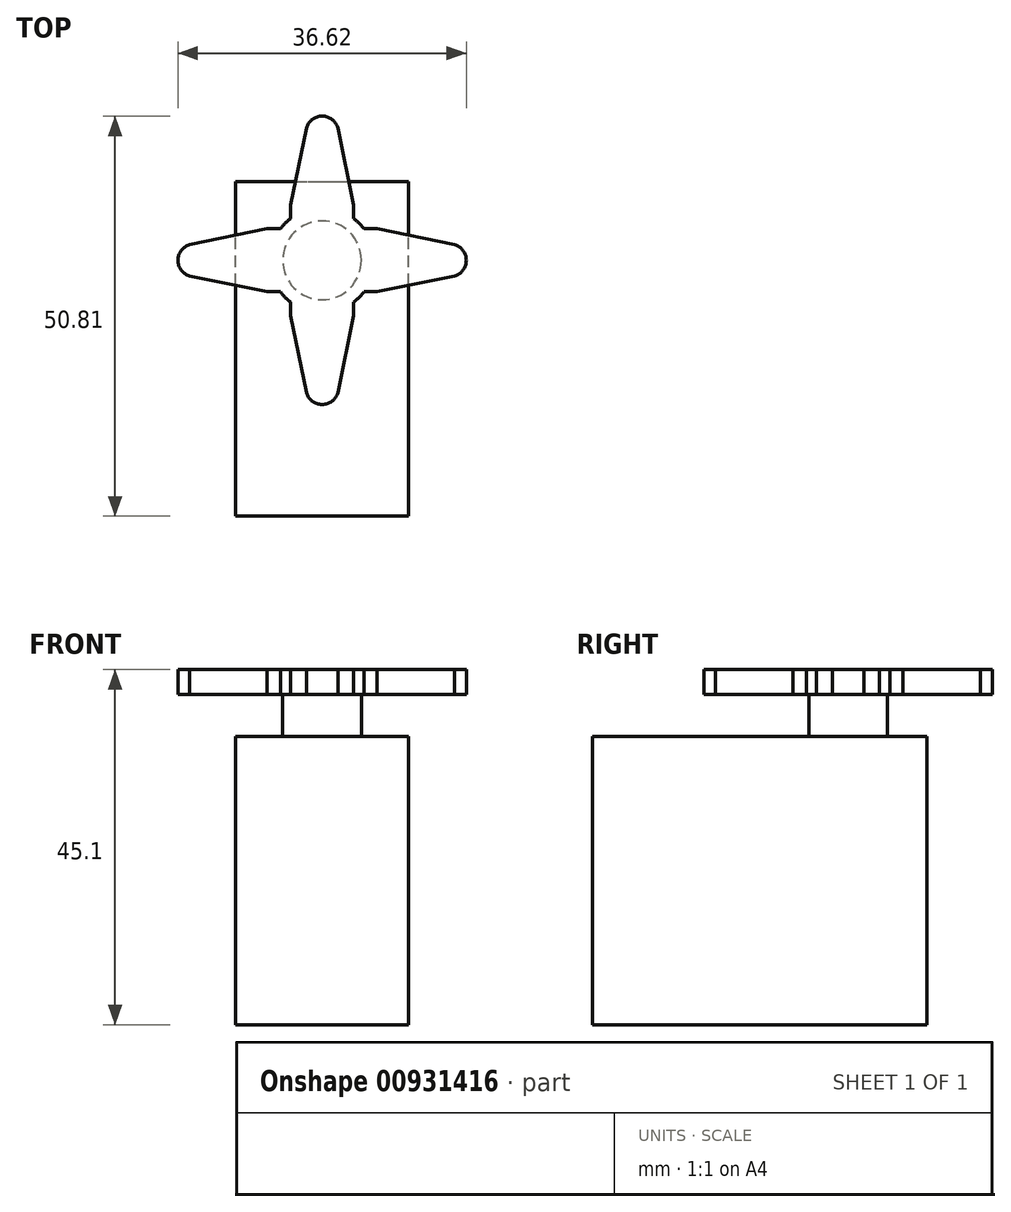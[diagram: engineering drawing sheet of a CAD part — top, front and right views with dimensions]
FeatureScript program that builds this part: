
annotation { "Feature Type Name" : "Feature", "Feature Type Description" : "" }
export const myFeature = defineFeature(function(context is Context, id is Id, definition is map)
    precondition{}
    {
        {
            var Q0;
            Q0=qCreatedBy(makeId("Top.planeOp"),FACE);
            var sketch = newSketch(context, id + "F0", { "sketchPlane" : qUnion([Q0])});
            skLineSegment(sketch, "E0.bottom", {"start": v(0, 0) * mm, "end": v(22, 0) * mm});
            skLineSegment(sketch, "E0.top", {"start": v(0, 42.5) * mm, "end": v(22, 42.5) * mm});
            skLineSegment(sketch, "E0.left", {"start": v(0, 0) * mm, "end": v(0, 42.5) * mm});
            skLineSegment(sketch, "E0.right", {"start": v(22, 0) * mm, "end": v(22, 42.5) * mm});
            skSolve(sketch);
        }
        {
            var Q0;
            Q0=makeQuery(id+"F0.imprint","IMPRINT",FACE,{"disambiguationData":[TD([[makeQuery(id+"F0.imprint","IMPRINT",EDGE,{"derivedFrom":sQuery(id+"F0.wireOp",EDGE,"E0.bottom")}),1.0]])]});
            extrude(context, id + "F1", {"entities" : qUnion([Q0]), "depth" : 36.6 * mm, "offsetDistance" : 25.4 * mm});
        }
        {
            var Q0;
            Q0=makeQuery(id+"F1.opExtrude","CAP_FACE",FACE,{"disambiguationData":[OSD([sQuery(id+"F0.wireOp",EDGE,"E0.bottom"),sQuery(id+"F0.wireOp",EDGE,"E0.top"),sQuery(id+"F0.wireOp",EDGE,"E0.left"),sQuery(id+"F0.wireOp",EDGE,"E0.right")])],"isStart":false});
            var sketch = newSketch(context, id + "F2", { "sketchPlane" : qUnion([Q0])});
            skLineSegment(sketch, "E1", {"start": v(11, 42.5) * mm, "end": v(11, 0) * mm, "construction": true});
            skCircle(sketch, "E2", {"center": v(11, 32.5) * mm, "radius": 5 * mm});
            skSolve(sketch);
        }
        {
            var Q0;
            Q0=makeQuery(id+"F2.imprint","IMPRINT",FACE,{"disambiguationData":[TD([[makeQuery(id+"F2.imprint","IMPRINT",EDGE,{"derivedFrom":sQuery(id+"F2.wireOp",EDGE,"E2")}),1.0]])]});
            extrude(context, id + "F3", {"entities" : qUnion([Q0]), "operationType" : NewBodyOperationType.ADD, "depth" : 8.5 * mm, "offsetDistance" : 25.4 * mm});
        }
        {
            var Q0;
            Q0=makeQuery(id+"F3.opExtrude","CAP_FACE",FACE,{"disambiguationData":[OSD([sQuery(id+"F2.wireOp",EDGE,"E2")])],"isStart":false});
            cPlane(context, id + "F4", {"entities" : qUnion([Q0]), "cplaneType" : CPlaneType.OFFSET, "offset" : 0 * mm, "width" : 152.4 * mm, "height" : 152.4 * mm});
        }
        {
            var Q0;
            Q0=qCreatedBy(id+"F4.planeOp",FACE);
            var sketch = newSketch(context, id + "F5", { "sketchPlane" : qUnion([Q0])});
            skCircle(sketch, "E3", {"center": v(11, 32.5) * mm, "radius": 6.65 * mm});
            skLineSegment(sketch, "E4", {"start": v(7, 37.81) * mm, "end": v(15, 37.81) * mm});
            skLineSegment(sketch, "E5", {"start": v(11, 37.81) * mm, "end": v(11, 50.81) * mm, "construction": true});
            skLineSegment(sketch, "E6", {"start": v(9, 49.31) * mm, "end": v(13, 49.31) * mm, "construction": true});
            skArc(sketch, "E7", {"start": v(13, 49.31) * mm, "mid": v(11, 50.81) * mm, "end": v(9, 49.31) * mm});
            skLineSegment(sketch, "E8", {"start": v(7, 39.5) * mm, "end": v(15, 39.5) * mm, "construction": true});
            skLineSegment(sketch, "E9", {"start": v(9, 49.31) * mm, "end": v(7, 39.5) * mm});
            skLineSegment(sketch, "E10", {"start": v(13, 49.31) * mm, "end": v(15, 39.5) * mm});
            skLineSegment(sketch, "E11", {"start": v(7, 39.5) * mm, "end": v(7, 37.81) * mm});
            skLineSegment(sketch, "E12", {"start": v(15, 39.5) * mm, "end": v(15, 37.81) * mm});
            skSolve(sketch);
        }
        {
            var Q0;
            {var subQ0=sQuery(id+"F5.wireOp",EDGE,"E4");Q0=makeQuery(id+"F5.imprint","IMPRINT",FACE,{"disambiguationData":[TD([[makeQuery(id+"F5.imprint","IMPRINT",EDGE,{"derivedFrom":subQ0}),-1.0]])]});}
            var Q1;
            {var subQ0=sQuery(id+"F5.wireOp",EDGE,"E4");Q1=makeQuery(id+"F5.imprint","IMPRINT",FACE,{"disambiguationData":[TD([[makeQuery(id+"F5.imprint","IMPRINT",EDGE,{"derivedFrom":subQ0}),1.0]])]});}
            extrude(context, id + "F6", {"entities" : qUnion([Q0, Q1]), "operationType" : NewBodyOperationType.ADD, "oppositeDirection" : true, "depth" : 3.17 * mm, "offsetDistance" : 25.4 * mm});
        }
        {
            var Q0;
            Q0=makeQuery(id+"F5.imprint","IMPRINT",FACE,{"disambiguationData":[TD([[makeQuery(id+"F5.imprint","IMPRINT",EDGE,{"derivedFrom":sQuery(id+"F5.wireOp",EDGE,"E7")}),1.0]])]});
            extrude(context, id + "F7", {"entities" : qUnion([Q0]), "oppositeDirection" : true, "depth" : 3.17 * mm, "offsetDistance" : 25.4 * mm});
        }
        {
            var Q0;
            Q0=makeQuery(id+"F7.opExtrude","SWEPT_BODY",BODY,{"disambiguationData":[OSD([sQuery(id+"F5.wireOp",EDGE,"E3"),sQuery(id+"F5.wireOp",EDGE,"E7"),sQuery(id+"F5.wireOp",EDGE,"E9"),sQuery(id+"F5.wireOp",EDGE,"E10"),sQuery(id+"F5.wireOp",EDGE,"E11"),sQuery(id+"F5.wireOp",EDGE,"E12")])]});
            var Q1;
            Q1=sQuery(id+"F5.wireOp",EDGE,"E3");
            circularPattern(context, id + "F8", {"operationType" : NewBodyOperationType.ADD, "entities" : qUnion([Q0]), "axis" : qUnion([Q1]), "angle" : 360 * degree, "instanceCount" : 4, "equalSpace" : true});
        }
    });
